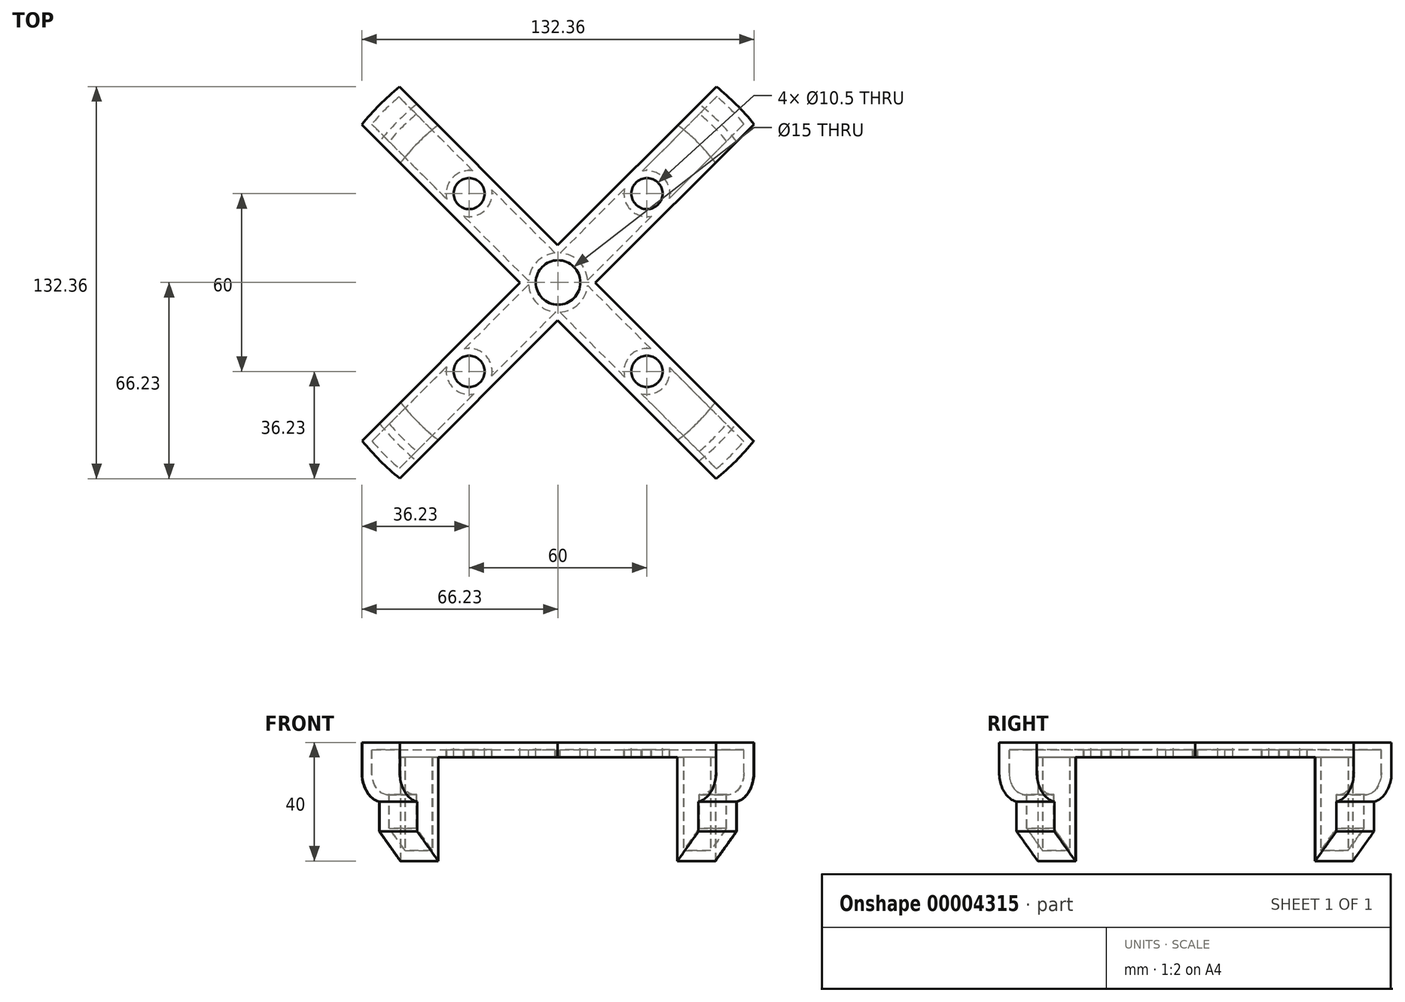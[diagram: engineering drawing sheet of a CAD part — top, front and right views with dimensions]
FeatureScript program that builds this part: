
annotation { "Feature Type Name" : "Feature", "Feature Type Description" : "" }
export const myFeature = defineFeature(function(context is Context, id is Id, definition is map)
    precondition{}
    {
        {
            var Q0;
            Q0=qCreatedBy(makeId("Top.planeOp"),FACE);
            var sketch = newSketch(context, id + "F0", { "sketchPlane" : qUnion([Q0])});
            skLineSegment(sketch, "E0", {"start": v(0, 0) * mm, "end": v(-30, 0) * mm, "construction": true});
            skLineSegment(sketch, "E1", {"start": v(0, 0) * mm, "end": v(30, 0) * mm, "construction": true});
            skLineSegment(sketch, "E2", {"start": v(0, 0) * mm, "end": v(0, -30) * mm, "construction": true});
            skLineSegment(sketch, "E3", {"start": v(0, 0) * mm, "end": v(0, 30) * mm, "construction": true});
            skLineSegment(sketch, "E4.0", {"start": v(0, 30) * mm, "end": v(-30, 30) * mm, "construction": true});
            skLineSegment(sketch, "E4.1", {"start": v(0, 30) * mm, "end": v(30, 30) * mm, "construction": true});
            skLineSegment(sketch, "E5.0", {"start": v(0, -30) * mm, "end": v(-30, -30) * mm, "construction": true});
            skLineSegment(sketch, "E5.1", {"start": v(0, -30) * mm, "end": v(30, -30) * mm, "construction": true});
            skLineSegment(sketch, "E6.0", {"start": v(-30, 0) * mm, "end": v(-30, -30) * mm, "construction": true});
            skLineSegment(sketch, "E6.1", {"start": v(-30, 0) * mm, "end": v(-30, 30) * mm, "construction": true});
            skLineSegment(sketch, "E7.0", {"start": v(30, 0) * mm, "end": v(30, -30) * mm, "construction": true});
            skLineSegment(sketch, "E7.1", {"start": v(30, 0) * mm, "end": v(30, 30) * mm, "construction": true});
            skCircle(sketch, "E8", {"center": v(-30, -30) * mm, "radius": 5.25 * mm});
            skCircle(sketch, "E9", {"center": v(30, -30) * mm, "radius": 5.25 * mm});
            skCircle(sketch, "E10", {"center": v(30, 30) * mm, "radius": 5.25 * mm});
            skCircle(sketch, "E11", {"center": v(-30, 30) * mm, "radius": 5.25 * mm});
            skSolve(sketch);
        }
        {
            var Q0;
            Q0=qCreatedBy(makeId("Top.planeOp"),FACE);
            var sketch = newSketch(context, id + "F1", { "sketchPlane" : qUnion([Q0])});
            skCircle(sketch, "E12", {"center": v(0, 0) * mm, "radius": 85 * mm});
            skSolve(sketch);
        }
        {
            var Q0;
            Q0=makeQuery(id+"F1.imprint","IMPRINT",FACE,{"disambiguationData":[TD([[makeQuery(id+"F1.imprint","IMPRINT",EDGE,{"derivedFrom":sQuery(id+"F1.wireOp",EDGE,"E12")}),1.0]])]});
            extrude(context, id + "F2", {"entities" : qUnion([Q0]), "oppositeDirection" : true, "depth" : 20 * mm});
        }
        {
            var Q0;
            Q0=makeQuery(id+"F0.imprint","IMPRINT",FACE,{"disambiguationData":[TD([[makeQuery(id+"F0.imprint","IMPRINT",EDGE,{"derivedFrom":sQuery(id+"F0.wireOp",EDGE,"E8")}),1.0]])]});
            var Q1;
            Q1=makeQuery(id+"F0.imprint","IMPRINT",FACE,{"disambiguationData":[TD([[makeQuery(id+"F0.imprint","IMPRINT",EDGE,{"derivedFrom":sQuery(id+"F0.wireOp",EDGE,"E9")}),1.0]])]});
            var Q2;
            Q2=makeQuery(id+"F0.imprint","IMPRINT",FACE,{"disambiguationData":[TD([[makeQuery(id+"F0.imprint","IMPRINT",EDGE,{"derivedFrom":sQuery(id+"F0.wireOp",EDGE,"E10")}),1.0]])]});
            var Q3;
            Q3=makeQuery(id+"F0.imprint","IMPRINT",FACE,{"disambiguationData":[TD([[makeQuery(id+"F0.imprint","IMPRINT",EDGE,{"derivedFrom":sQuery(id+"F0.wireOp",EDGE,"E11")}),1.0]])]});
            extrude(context, id + "F3", {"entities" : qUnion([Q0, Q1, Q2, Q3]), "operationType" : NewBodyOperationType.REMOVE, "oppositeDirection" : true, "depth" : 10 * mm});
        }
        {
            var Q0;
            Q0=makeQuery(id+"F2.opExtrude","CAP_FACE",FACE,{"disambiguationData":[OSD([sQuery(id+"F1.wireOp",EDGE,"E12")])],"isStart":false});
            var sketch = newSketch(context, id + "F4", { "sketchPlane" : qUnion([Q0])});
            skCircle(sketch, "E13", {"center": v(0, 0) * mm, "radius": 76.75 * mm});
            skSolve(sketch);
        }
        {
            var Q0;
            Q0=makeQuery(id+"F4.imprint","IMPRINT",FACE,{"disambiguationData":[TD([[makeQuery(id+"F4.imprint","IMPRINT",EDGE,{"derivedFrom":sQuery(id+"F4.wireOp",EDGE,"E13")}),1.0]])]});
            extrude(context, id + "F5", {"entities" : qUnion([Q0]), "operationType" : NewBodyOperationType.ADD, "depth" : 20 * mm});
        }
        {
            var Q0;
            Q0=makeQuery(id+"F2.opExtrude","CAP_EDGE",EDGE,{"disambiguationData":[OSD([sQuery(id+"F1.wireOp",EDGE,"E12")])],"isStart":false});
            fillet(context, id + "F6", {"entities" : qUnion([Q0]), "radius" : 10 * mm, "tangentPropagation" : true, "allowEdgeOverflow" : false});
        }
        {
            var Q0;
            Q0=makeQuery(id+"F5.opExtrude","CAP_FACE",FACE,{"disambiguationData":[OSD([sQuery(id+"F4.wireOp",EDGE,"E13")])],"isStart":false});
            chamfer(context, id + "F7", {"entities" : qUnion([Q0]), "width" : 10 * mm, "tangentPropagation" : true});
        }
        {
            var Q0;
            Q0=makeQuery(id+"F2.opExtrude","CAP_FACE",FACE,{"disambiguationData":[OSD([sQuery(id+"F1.wireOp",EDGE,"E12")])],"isStart":true});
            var sketch = newSketch(context, id + "F8", { "sketchPlane" : qUnion([Q0])});
            skCircle(sketch, "E14", {"center": v(0, 0) * mm, "radius": 7.5 * mm});
            skSolve(sketch);
        }
        {
            var Q0;
            Q0=makeQuery(id+"F8.imprint","IMPRINT",FACE,{"disambiguationData":[TD([[makeQuery(id+"F8.imprint","IMPRINT",EDGE,{"derivedFrom":sQuery(id+"F8.wireOp",EDGE,"E14")}),1.0]])]});
            extrude(context, id + "F9", {"entities" : qUnion([Q0]), "operationType" : NewBodyOperationType.REMOVE, "oppositeDirection" : true, "depth" : 130.55 * mm});
        }
        {
            var Q0;
            Q0=makeQuery(id+"F2.opExtrude","CAP_FACE",FACE,{"disambiguationData":[OSD([sQuery(id+"F1.wireOp",EDGE,"E12")])],"isStart":true});
            var sketch = newSketch(context, id + "F10", { "sketchPlane" : qUnion([Q0])});
            skLineSegment(sketch, "E15", {"start": v(150.33, -150.56) * mm, "end": v(-148.1, 147.88) * mm});
            skLineSegment(sketch, "E16", {"start": v(-148.1, 147.88) * mm, "end": v(-154.47, 141.51) * mm});
            skLineSegment(sketch, "E17", {"start": v(-148.1, 147.88) * mm, "end": v(-141.75, 154.24) * mm});
            skLineSegment(sketch, "E18", {"start": v(-148.22, -148.22) * mm, "end": v(-154.59, -141.86) * mm});
            skLineSegment(sketch, "E19", {"start": v(-148.22, -148.22) * mm, "end": v(-141.86, -154.59) * mm});
            skLineSegment(sketch, "E20", {"start": v(156.9, -144.4) * mm, "end": v(143.77, -156.72) * mm});
            skLineSegment(sketch, "E21", {"start": v(-148.22, -148.22) * mm, "end": v(151.43, 151.44) * mm});
            skLineSegment(sketch, "E22", {"start": v(151.43, 151.44) * mm, "end": v(157.8, 145.07) * mm});
            skLineSegment(sketch, "E23", {"start": v(151.43, 151.44) * mm, "end": v(145.07, 157.8) * mm});
            skLineSegment(sketch, "E24", {"start": v(-154.47, 141.51) * mm, "end": v(156.2, -169.15) * mm});
            skLineSegment(sketch, "E25", {"start": v(-141.75, 154.24) * mm, "end": v(181.35, -168.85) * mm});
            skLineSegment(sketch, "E26", {"start": v(-154.59, -141.86) * mm, "end": v(161.97, 174.7) * mm});
            skLineSegment(sketch, "E27", {"start": v(-141.86, -154.59) * mm, "end": v(180.9, 168.17) * mm});
            skSolve(sketch);
        }
        {
            var Q0;
            {var subQ1=sQuery(id+"F10.wireOp",EDGE,"E26");var subQ3=sQuery(id+"F10.wireOp",EDGE,"E24");var subQ5=makeQuery(id+"F10.imprint","INTERSECT",VERTEX,{"derivedFrom":[subQ3,subQ1]});Q0=makeQuery(id+"F10.imprint","IMPRINT",FACE,{"disambiguationData":[TD([[makeQuery(id+"F10.imprint","IMPRINT",EDGE,{"disambiguationData":[TD([[subQ5,1.0]])],"derivedFrom":subQ3}),-1.0]])]});}
            var Q1;
            {var subQ1=sQuery(id+"F10.wireOp",EDGE,"E26");var subQ3=sQuery(id+"F10.wireOp",EDGE,"E25");var subQ5=makeQuery(id+"F10.imprint","INTERSECT",VERTEX,{"derivedFrom":[subQ3,subQ1]});Q1=makeQuery(id+"F10.imprint","IMPRINT",FACE,{"disambiguationData":[TD([[makeQuery(id+"F10.imprint","IMPRINT",EDGE,{"disambiguationData":[TD([[subQ5,1.0]])],"derivedFrom":subQ3}),1.0]])]});}
            var Q2;
            {var subQ1=sQuery(id+"F10.wireOp",EDGE,"E27");var subQ3=sQuery(id+"F10.wireOp",EDGE,"E25");var subQ5=makeQuery(id+"F10.imprint","INTERSECT",VERTEX,{"derivedFrom":[subQ3,subQ1]});Q2=makeQuery(id+"F10.imprint","IMPRINT",FACE,{"disambiguationData":[TD([[makeQuery(id+"F10.imprint","IMPRINT",EDGE,{"disambiguationData":[TD([[subQ5,-1.0]])],"derivedFrom":subQ3}),1.0]])]});}
            var Q3;
            {var subQ1=sQuery(id+"F10.wireOp",EDGE,"E27");var subQ3=sQuery(id+"F10.wireOp",EDGE,"E24");var subQ5=makeQuery(id+"F10.imprint","INTERSECT",VERTEX,{"derivedFrom":[subQ3,subQ1]});Q3=makeQuery(id+"F10.imprint","IMPRINT",FACE,{"disambiguationData":[TD([[makeQuery(id+"F10.imprint","IMPRINT",EDGE,{"disambiguationData":[TD([[subQ5,-1.0]])],"derivedFrom":subQ3}),-1.0]])]});}
            extrude(context, id + "F11", {"entities" : qUnion([Q0, Q1, Q2, Q3]), "operationType" : NewBodyOperationType.REMOVE, "oppositeDirection" : true, "depth" : 74.84 * mm});
        }
        {
            var Q0;
            Q0=makeQuery(id+"F5.opExtrude","CAP_FACE",FACE,{"disambiguationData":[OSD([sQuery(id+"F4.wireOp",EDGE,"E13")])],"isStart":false});
            var sketch = newSketch(context, id + "F12", { "sketchPlane" : qUnion([Q0])});
            skCircle(sketch, "E28", {"center": v(-0.11, 0) * mm, "radius": 49.41 * mm});
            skSolve(sketch);
        }
        {
            var Q0;
            {var subQ0=makeQuery(id+"F5.opExtrude","CAP_FACE",FACE,{"disambiguationData":[OSD([sQuery(id+"F4.wireOp",EDGE,"E13")])],"isStart":false});Q0=makeQuery(id+"F12.imprint","IMPRINT",FACE,{"disambiguationData":[TD([[makeQuery(id+"F12.imprint","IMPRINT",EDGE,{"derivedFrom":makeQuery(id+"F9.boolean.opBoolean","INTERSECT",EDGE,{"derivedFrom":[subQ0,makeQuery(id+"F9.opExtrude","SWEPT_FACE",FACE,{"disambiguationData":[OSD([sQuery(id+"F8.wireOp",EDGE,"E14")])]})]})}),-1.0]])]});}
            extrude(context, id + "F13", {"entities" : qUnion([Q0]), "operationType" : NewBodyOperationType.REMOVE, "oppositeDirection" : true, "depth" : 35 * mm});
        }
        {
            var Q0;
            {var subQ0=sQuery(id+"F4.wireOp",EDGE,"E13");var subQ1=makeQuery(id+"F5.opExtrude","CAP_FACE",FACE,{"disambiguationData":[OSD([subQ0])],"isStart":false});var subQ5=sQuery(id+"F10.wireOp",EDGE,"E26");var subQ7=sQuery(id+"F10.wireOp",EDGE,"E24");var subQ8=makeQuery(id+"F11.opExtrude","SWEPT_FACE",FACE,{"disambiguationData":[OSD([subQ7]),TDD([makeQuery(id+"F10.imprint","IMPRINT",EDGE,{"disambiguationData":[TD([[makeQuery(id+"F10.imprint","INTERSECT",VERTEX,{"derivedFrom":[subQ7,subQ5]}),1.0]])],"derivedFrom":subQ7})])]});Q0=makeQuery(id+"F13.boolean.opBoolean","SPLIT",FACE,{"disambiguationData":[TD([makeQuery(id+"F11.boolean.opBoolean","COPY",FACE,{"derivedFrom":subQ8})])],"derivedFrom":subQ1});}
            var Q1;
            {var subQ0=sQuery(id+"F4.wireOp",EDGE,"E13");var subQ1=makeQuery(id+"F5.opExtrude","CAP_FACE",FACE,{"disambiguationData":[OSD([subQ0])],"isStart":false});var subQ3=sQuery(id+"F10.wireOp",EDGE,"E26");var subQ5=sQuery(id+"F10.wireOp",EDGE,"E24");var subQ6=makeQuery(id+"F11.opExtrude","SWEPT_FACE",FACE,{"disambiguationData":[OSD([subQ3]),TDD([makeQuery(id+"F10.imprint","IMPRINT",EDGE,{"disambiguationData":[TD([[makeQuery(id+"F10.imprint","INTERSECT",VERTEX,{"derivedFrom":[subQ5,subQ3]}),1.0]])],"derivedFrom":subQ3})])]});Q1=makeQuery(id+"F13.boolean.opBoolean","SPLIT",FACE,{"disambiguationData":[TD([makeQuery(id+"F11.boolean.opBoolean","COPY",FACE,{"derivedFrom":subQ6})])],"derivedFrom":subQ1});}
            var Q2;
            {var subQ0=sQuery(id+"F4.wireOp",EDGE,"E13");var subQ1=makeQuery(id+"F5.opExtrude","CAP_FACE",FACE,{"disambiguationData":[OSD([subQ0])],"isStart":false});var subQ5=sQuery(id+"F10.wireOp",EDGE,"E27");var subQ7=sQuery(id+"F10.wireOp",EDGE,"E24");var subQ8=makeQuery(id+"F11.opExtrude","SWEPT_FACE",FACE,{"disambiguationData":[OSD([subQ7]),TDD([makeQuery(id+"F10.imprint","IMPRINT",EDGE,{"disambiguationData":[TD([[makeQuery(id+"F10.imprint","INTERSECT",VERTEX,{"derivedFrom":[subQ7,subQ5]}),-1.0]])],"derivedFrom":subQ7})])]});Q2=makeQuery(id+"F13.boolean.opBoolean","SPLIT",FACE,{"disambiguationData":[TD([makeQuery(id+"F11.boolean.opBoolean","COPY",FACE,{"derivedFrom":subQ8})])],"derivedFrom":subQ1});}
            var Q3;
            {var subQ0=sQuery(id+"F4.wireOp",EDGE,"E13");var subQ1=makeQuery(id+"F5.opExtrude","CAP_FACE",FACE,{"disambiguationData":[OSD([subQ0])],"isStart":false});var subQ5=sQuery(id+"F10.wireOp",EDGE,"E25");var subQ7=sQuery(id+"F10.wireOp",EDGE,"E26");var subQ8=makeQuery(id+"F11.opExtrude","SWEPT_FACE",FACE,{"disambiguationData":[OSD([subQ7]),TDD([makeQuery(id+"F10.imprint","IMPRINT",EDGE,{"disambiguationData":[TD([[makeQuery(id+"F10.imprint","INTERSECT",VERTEX,{"derivedFrom":[subQ5,subQ7]}),-1.0]])],"derivedFrom":subQ7})])]});Q3=makeQuery(id+"F13.boolean.opBoolean","SPLIT",FACE,{"disambiguationData":[TD([makeQuery(id+"F11.boolean.opBoolean","COPY",FACE,{"derivedFrom":subQ8})])],"derivedFrom":subQ1});}
            var Q4;
            Q4=makeQuery(id+"F13.boolean.opBoolean","COPY",FACE,{"derivedFrom":makeQuery(id+"F13.opExtrude","CAP_FACE",FACE,{"disambiguationData":[OSD([sQuery(id+"F4.wireOp",EDGE,"E13"),sQuery(id+"F8.wireOp",EDGE,"E14"),sQuery(id+"F10.wireOp",EDGE,"E24"),sQuery(id+"F10.wireOp",EDGE,"E25"),sQuery(id+"F10.wireOp",EDGE,"E26"),sQuery(id+"F10.wireOp",EDGE,"E27"),sQuery(id+"F12.wireOp",EDGE,"E28")])],"isStart":false})});
            shell(context, id + "F14", {"entities" : qUnion([Q0, Q1, Q2, Q3, Q4]), "thickness" : 2.5 * mm});
        }
        {
            var Q0;
            {var subQ0=sQuery(id+"F4.wireOp",EDGE,"E13");var subQ1=makeQuery(id+"F5.opExtrude","CAP_FACE",FACE,{"disambiguationData":[OSD([subQ0])],"isStart":false});var subQ5=sQuery(id+"F10.wireOp",EDGE,"E27");var subQ7=sQuery(id+"F10.wireOp",EDGE,"E24");var subQ8=makeQuery(id+"F11.opExtrude","SWEPT_FACE",FACE,{"disambiguationData":[OSD([subQ7]),TDD([makeQuery(id+"F10.imprint","IMPRINT",EDGE,{"disambiguationData":[TD([[makeQuery(id+"F10.imprint","INTERSECT",VERTEX,{"derivedFrom":[subQ7,subQ5]}),-1.0]])],"derivedFrom":subQ7})])]});Q0=makeQuery(id+"F13.boolean.opBoolean","SPLIT",FACE,{"disambiguationData":[TD([makeQuery(id+"F11.boolean.opBoolean","COPY",FACE,{"derivedFrom":subQ8})])],"derivedFrom":subQ1});}
            var Q1;
            {var subQ0=sQuery(id+"F4.wireOp",EDGE,"E13");var subQ1=makeQuery(id+"F5.opExtrude","CAP_FACE",FACE,{"disambiguationData":[OSD([subQ0])],"isStart":false});var subQ5=sQuery(id+"F10.wireOp",EDGE,"E25");var subQ7=sQuery(id+"F10.wireOp",EDGE,"E26");var subQ8=makeQuery(id+"F11.opExtrude","SWEPT_FACE",FACE,{"disambiguationData":[OSD([subQ7]),TDD([makeQuery(id+"F10.imprint","IMPRINT",EDGE,{"disambiguationData":[TD([[makeQuery(id+"F10.imprint","INTERSECT",VERTEX,{"derivedFrom":[subQ5,subQ7]}),-1.0]])],"derivedFrom":subQ7})])]});Q1=makeQuery(id+"F13.boolean.opBoolean","SPLIT",FACE,{"disambiguationData":[TD([makeQuery(id+"F11.boolean.opBoolean","COPY",FACE,{"derivedFrom":subQ8})])],"derivedFrom":subQ1});}
            var Q2;
            {var subQ0=sQuery(id+"F4.wireOp",EDGE,"E13");var subQ1=makeQuery(id+"F5.opExtrude","CAP_FACE",FACE,{"disambiguationData":[OSD([subQ0])],"isStart":false});var subQ5=sQuery(id+"F10.wireOp",EDGE,"E26");var subQ7=sQuery(id+"F10.wireOp",EDGE,"E24");var subQ8=makeQuery(id+"F11.opExtrude","SWEPT_FACE",FACE,{"disambiguationData":[OSD([subQ7]),TDD([makeQuery(id+"F10.imprint","IMPRINT",EDGE,{"disambiguationData":[TD([[makeQuery(id+"F10.imprint","INTERSECT",VERTEX,{"derivedFrom":[subQ7,subQ5]}),1.0]])],"derivedFrom":subQ7})])]});Q2=makeQuery(id+"F13.boolean.opBoolean","SPLIT",FACE,{"disambiguationData":[TD([makeQuery(id+"F11.boolean.opBoolean","COPY",FACE,{"derivedFrom":subQ8})])],"derivedFrom":subQ1});}
            var Q3;
            {var subQ0=sQuery(id+"F4.wireOp",EDGE,"E13");var subQ1=makeQuery(id+"F5.opExtrude","CAP_FACE",FACE,{"disambiguationData":[OSD([subQ0])],"isStart":false});var subQ3=sQuery(id+"F10.wireOp",EDGE,"E26");var subQ5=sQuery(id+"F10.wireOp",EDGE,"E24");var subQ6=makeQuery(id+"F11.opExtrude","SWEPT_FACE",FACE,{"disambiguationData":[OSD([subQ3]),TDD([makeQuery(id+"F10.imprint","IMPRINT",EDGE,{"disambiguationData":[TD([[makeQuery(id+"F10.imprint","INTERSECT",VERTEX,{"derivedFrom":[subQ5,subQ3]}),1.0]])],"derivedFrom":subQ3})])]});Q3=makeQuery(id+"F13.boolean.opBoolean","SPLIT",FACE,{"disambiguationData":[TD([makeQuery(id+"F11.boolean.opBoolean","COPY",FACE,{"derivedFrom":subQ6})])],"derivedFrom":subQ1});}
            extrude(context, id + "F15", {"entities" : qUnion([Q0, Q1, Q2, Q3]), "operationType" : NewBodyOperationType.REMOVE, "oppositeDirection" : true, "depth" : 15 * mm});
        }
        {
            var Q0;
            {var subQ0=sQuery(id+"F4.wireOp",EDGE,"E13");var subQ1=makeQuery(id+"F5.opExtrude","CAP_FACE",FACE,{"disambiguationData":[OSD([subQ0])],"isStart":false});var subQ3=sQuery(id+"F10.wireOp",EDGE,"E26");var subQ5=sQuery(id+"F10.wireOp",EDGE,"E24");var subQ6=makeQuery(id+"F11.opExtrude","SWEPT_FACE",FACE,{"disambiguationData":[OSD([subQ3]),TDD([makeQuery(id+"F10.imprint","IMPRINT",EDGE,{"disambiguationData":[TD([[makeQuery(id+"F10.imprint","INTERSECT",VERTEX,{"derivedFrom":[subQ5,subQ3]}),1.0]])],"derivedFrom":subQ3})])]});Q0=makeQuery(id+"F15.boolean.opBoolean","COPY",FACE,{"derivedFrom":makeQuery(id+"F15.opExtrude","CAP_FACE",FACE,{"disambiguationData":[OSD([subQ0]),TDD([makeQuery(id+"F13.boolean.opBoolean","SPLIT",FACE,{"disambiguationData":[TD([makeQuery(id+"F11.boolean.opBoolean","COPY",FACE,{"derivedFrom":subQ6})])],"derivedFrom":subQ1})])],"isStart":false})});}
            var Q1;
            {var subQ0=sQuery(id+"F4.wireOp",EDGE,"E13");var subQ1=makeQuery(id+"F5.opExtrude","CAP_FACE",FACE,{"disambiguationData":[OSD([subQ0])],"isStart":false});var subQ5=sQuery(id+"F10.wireOp",EDGE,"E27");var subQ7=sQuery(id+"F10.wireOp",EDGE,"E24");var subQ8=makeQuery(id+"F11.opExtrude","SWEPT_FACE",FACE,{"disambiguationData":[OSD([subQ7]),TDD([makeQuery(id+"F10.imprint","IMPRINT",EDGE,{"disambiguationData":[TD([[makeQuery(id+"F10.imprint","INTERSECT",VERTEX,{"derivedFrom":[subQ7,subQ5]}),-1.0]])],"derivedFrom":subQ7})])]});Q1=makeQuery(id+"F15.boolean.opBoolean","COPY",FACE,{"derivedFrom":makeQuery(id+"F15.opExtrude","CAP_FACE",FACE,{"disambiguationData":[OSD([subQ0]),TDD([makeQuery(id+"F13.boolean.opBoolean","SPLIT",FACE,{"disambiguationData":[TD([makeQuery(id+"F11.boolean.opBoolean","COPY",FACE,{"derivedFrom":subQ8})])],"derivedFrom":subQ1})])],"isStart":false})});}
            var Q2;
            {var subQ0=sQuery(id+"F4.wireOp",EDGE,"E13");var subQ1=makeQuery(id+"F5.opExtrude","CAP_FACE",FACE,{"disambiguationData":[OSD([subQ0])],"isStart":false});var subQ5=sQuery(id+"F10.wireOp",EDGE,"E26");var subQ7=sQuery(id+"F10.wireOp",EDGE,"E24");var subQ8=makeQuery(id+"F11.opExtrude","SWEPT_FACE",FACE,{"disambiguationData":[OSD([subQ7]),TDD([makeQuery(id+"F10.imprint","IMPRINT",EDGE,{"disambiguationData":[TD([[makeQuery(id+"F10.imprint","INTERSECT",VERTEX,{"derivedFrom":[subQ7,subQ5]}),1.0]])],"derivedFrom":subQ7})])]});Q2=makeQuery(id+"F15.boolean.opBoolean","COPY",FACE,{"derivedFrom":makeQuery(id+"F15.opExtrude","CAP_FACE",FACE,{"disambiguationData":[OSD([subQ0]),TDD([makeQuery(id+"F13.boolean.opBoolean","SPLIT",FACE,{"disambiguationData":[TD([makeQuery(id+"F11.boolean.opBoolean","COPY",FACE,{"derivedFrom":subQ8})])],"derivedFrom":subQ1})])],"isStart":false})});}
            var Q3;
            {var subQ0=sQuery(id+"F4.wireOp",EDGE,"E13");var subQ1=makeQuery(id+"F5.opExtrude","CAP_FACE",FACE,{"disambiguationData":[OSD([subQ0])],"isStart":false});var subQ5=sQuery(id+"F10.wireOp",EDGE,"E25");var subQ7=sQuery(id+"F10.wireOp",EDGE,"E26");var subQ8=makeQuery(id+"F11.opExtrude","SWEPT_FACE",FACE,{"disambiguationData":[OSD([subQ7]),TDD([makeQuery(id+"F10.imprint","IMPRINT",EDGE,{"disambiguationData":[TD([[makeQuery(id+"F10.imprint","INTERSECT",VERTEX,{"derivedFrom":[subQ5,subQ7]}),-1.0]])],"derivedFrom":subQ7})])]});Q3=makeQuery(id+"F15.boolean.opBoolean","COPY",FACE,{"derivedFrom":makeQuery(id+"F15.opExtrude","CAP_FACE",FACE,{"disambiguationData":[OSD([subQ0]),TDD([makeQuery(id+"F13.boolean.opBoolean","SPLIT",FACE,{"disambiguationData":[TD([makeQuery(id+"F11.boolean.opBoolean","COPY",FACE,{"derivedFrom":subQ8})])],"derivedFrom":subQ1})])],"isStart":false})});}
            extrude(context, id + "F16", {"entities" : qUnion([Q0, Q1, Q2, Q3]), "operationType" : NewBodyOperationType.REMOVE, "oppositeDirection" : true, "depth" : 20 * mm});
        }
    });
